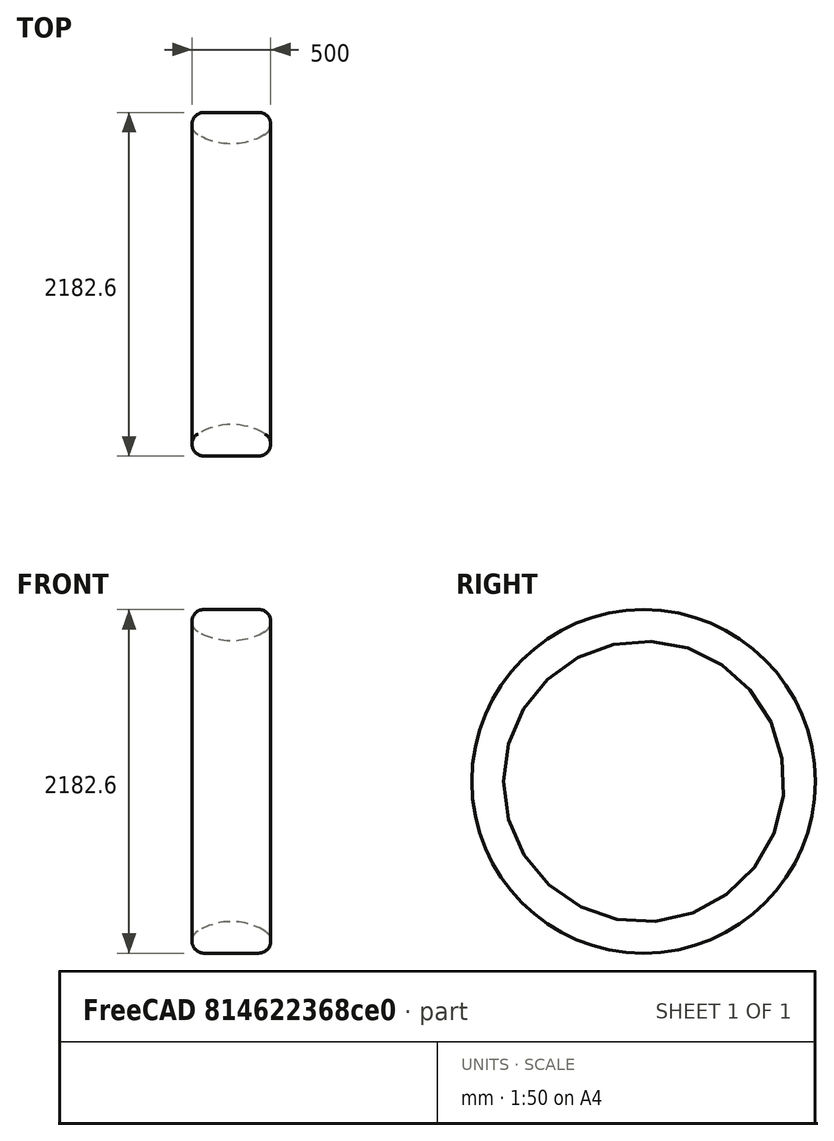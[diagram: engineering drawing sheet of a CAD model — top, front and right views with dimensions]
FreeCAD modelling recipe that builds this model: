
FCSTD DOCUMENT
Label: 3_Profile0_rHWR1
objects: Sketcher::SketchObject×1, PartDesign::Revolution×1
note: 3 computed .brp shape members not serialized (recipe doc carries the construction recipe); baked Part::Feature solids carry a one-line shape summary decoded from their .brp

FEATURE [Sketcher::SketchObject] Sketch
  sketch-geometry (7):
    g0: LineSegment StartX=-230.408 StartY=-1091.3 StartZ=0 EndX=117.592 EndY=-1091.3 EndZ=0
    g1: ArcOfCircle CenterX=-230.408 CenterY=-1015.3 CenterZ=0 NormalX=0 NormalY=0 NormalZ=1 Radius=76 StartAngle=2.1062 EndAngle=4.71239
    g2: ArcOfCircle CenterX=117.592 CenterY=-1015.3 CenterZ=0 NormalX=0 NormalY=0 NormalZ=1 Radius=76 StartAngle=4.71239 EndAngle=7.31858
    g3: ArcOfCircle CenterX=-56.4078 CenterY=-1306.66 CenterZ=0 NormalX=0 NormalY=0 NormalZ=1 Radius=415.365 StartAngle=1.03539 EndAngle=2.1062
    g4: LineSegment StartX=-269.182 StartY=-949.935 StartZ=0 EndX=-268.322 EndY=-949.425 EndZ=0
    g5: LineSegment StartX=155.506 StartY=-949.425 StartZ=0 EndX=156.367 EndY=-949.935 EndZ=0
    g6: LineSegment [constr] StartX=-156.794 StartY=-891.3 StartZ=0 EndX=210.226 EndY=-891.3 EndZ=0
  constraints (16):
    c: Horizontal(g0)
    c: Tangent(g1,g0)
    c: Tangent(g0,g2)
    c: Radius(g1) = 76
    c: Radius(g2) = 76
    c: Tangent(g3,g4)
    c: Tangent(g1,g4)
    c: Tangent(g3,g5)
    c: Tangent(g5,g2)
    c: Distance(g4) = 1
    c: Distance(g5) = 1
    c: Horizontal(g6)
    c: Tangent(g6,g3)
    c: DistanceY(g6) = -891.3
    c: Distance(g1,g2) = 348
    c: Distance(g0,g6) = 200
FEATURE [PartDesign::Revolution] Revolution
  Angle = 360
  Axis = (1,0,0)
  Base = (0,0,0)
  Sketch = -> Sketch
